# Revit family: Shower-Shower_Column_Kit-KOHLER-Atom-K-30021T_1
name_source: partatom
category: Plumbing Fixtures
units: mm (PartAtom-declared; Revit-internal decimal feet)

## family parameters
Cut with Voids When Loaded = No
Host = Face
OmniClass Number = 23.31.17.00
OmniClass Title = Showers
Part Type = Normal
Room Calculation Point = No
Round Connector Dimension = Use Diameter
Shared = No

## types (1)
- CP-Polished Chrome
    ADA Compliant = No
    Assembly Code = D2010700
    CW Connection = Yes
    Cold Water Inlet = Cold Water Inlet
    Date Modified = 12/13/2022
    Default Elevation = 42"
    Description = Thermostatic Three Way Shower Column Direct 3P
    Drain Included = No
    Finish = Kohler-Metal-CP-Polished_Chrome
    Flow Rate = 0 GPM
    HW Connection = Yes
    Handle Clearance = 1 1/16"
    Height = 41 13/16"
    Hot Water Inlet = Hot Water Inlet
    Length = 21 1/2"
    Manufacturer = Kohler Co.
    Master Format 2014 = 22 42 23
    Master Format 2014 Name = Residential Showers
    Material = Premium Metal Construction
    Model = K-30021T-7-CP
    Pressure = 0.00 psi
    Product Name = Atom
    Spout Reach = 4 5/16"
    Type = 1
    URL = http://www.kohler.com.cn
    Vent Connection = No
    Waste Connection = No
    Waste Water Outlet = Waste Water Outlet
    WaterSense Certified = No
    Width = 11 13/16"

## geometry (parser evidence)
native form markers: Sweep x4
no freeform markers — native parametric forms only
